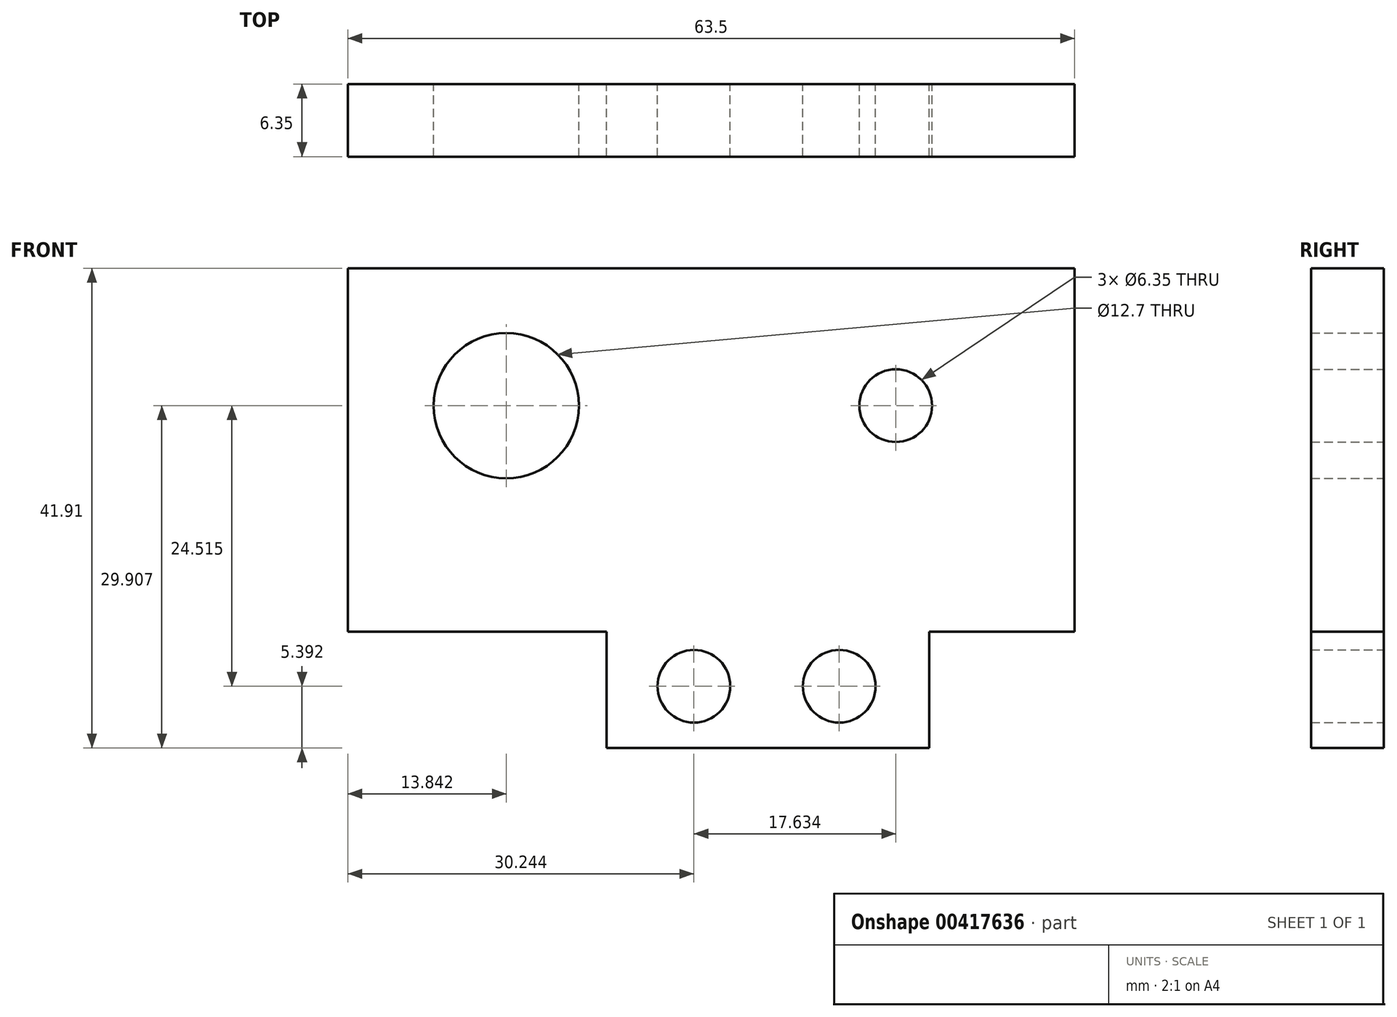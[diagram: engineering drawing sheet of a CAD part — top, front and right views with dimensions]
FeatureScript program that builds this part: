
annotation { "Feature Type Name" : "Feature", "Feature Type Description" : "" }
export const myFeature = defineFeature(function(context is Context, id is Id, definition is map)
    precondition{}
    {
        {
            var Q0;
            Q0=qCreatedBy(makeId("Front.planeOp"),FACE);
            var sketch = newSketch(context, id + "F0", { "sketchPlane" : qUnion([Q0])});
            skLineSegment(sketch, "E0", {"start": v(-23.02, 21.88) * mm, "end": v(40.48, 21.88) * mm});
            skLineSegment(sketch, "E1", {"start": v(-23.02, 21.88) * mm, "end": v(-23.02, -9.87) * mm});
            skLineSegment(sketch, "E2", {"start": v(-23.02, -9.87) * mm, "end": v(-0.4, -9.87) * mm});
            skLineSegment(sketch, "E3", {"start": v(-0.4, -9.87) * mm, "end": v(-0.4, -20.03) * mm});
            skLineSegment(sketch, "E4", {"start": v(-0.4, -20.03) * mm, "end": v(27.78, -20.03) * mm});
            skLineSegment(sketch, "E5", {"start": v(27.78, -20.03) * mm, "end": v(27.78, -9.87) * mm});
            skLineSegment(sketch, "E6", {"start": v(27.78, -9.87) * mm, "end": v(40.48, -9.87) * mm});
            skLineSegment(sketch, "E7", {"start": v(40.48, -9.87) * mm, "end": v(40.48, 21.88) * mm});
            skPoint(sketch, "E8.startSnap0", {"position": v(-11.71, -9.87) * mm});
            skPoint(sketch, "E9", {"position": v(7.22, -14.64) * mm});
            skPoint(sketch, "E10", {"position": v(19.92, -14.64) * mm});
            skPoint(sketch, "E11", {"position": v(-9.18, 9.88) * mm});
            skPoint(sketch, "E12", {"position": v(24.86, 9.88) * mm});
            skPoint(sketch, "E13", {"position": v(-0.4, -14.95) * mm});
            skPoint(sketch, "E14", {"position": v(27.78, -14.95) * mm});
            skLineSegment(sketch, "E15", {"start": v(-0.4, -14.95) * mm, "end": v(27.78, -14.95) * mm});
            skPoint(sketch, "E16", {"position": v(-23.02, 9.18) * mm});
            skPoint(sketch, "E17", {"position": v(40.48, 9.18) * mm});
            skLineSegment(sketch, "E18", {"start": v(-23.02, 9.18) * mm, "end": v(40.48, 9.18) * mm});
            skSolve(sketch);
        }
        {
            var Q0;
            Q0=makeQuery(id+"F0.imprint","IMPRINT",FACE,{"disambiguationData":[TD([[makeQuery(id+"F0.imprint","IMPRINT",EDGE,{"derivedFrom":sQuery(id+"F0.wireOp",EDGE,"E0")}),-1.0]])]});
            var Q1;
            {var subQ1=sQuery(id+"F0.wireOp",EDGE,"E2");Q1=makeQuery(id+"F0.imprint","IMPRINT",FACE,{"disambiguationData":[TD([[makeQuery(id+"F0.imprint","IMPRINT",EDGE,{"derivedFrom":subQ1}),1.0]])]});}
            var Q2;
            {var subQ0=sQuery(id+"F0.wireOp",EDGE,"E4");Q2=makeQuery(id+"F0.imprint","IMPRINT",FACE,{"disambiguationData":[TD([[makeQuery(id+"F0.imprint","IMPRINT",EDGE,{"derivedFrom":subQ0}),1.0]])]});}
            extrude(context, id + "F1", {"entities" : qUnion([Q0, Q1, Q2]), "depth" : 6.35 * mm});
        }
        {
            var Q0;
            Q0=sQuery(id+"F0.wireOp",VERTEX,"E11");
            var Q1;
            Q1=makeQuery(id+"F1.opExtrude","SWEPT_BODY",BODY,{"disambiguationData":[OSD([sQuery(id+"F0.wireOp",EDGE,"E0"),sQuery(id+"F0.wireOp",EDGE,"E1"),sQuery(id+"F0.wireOp",EDGE,"E2"),sQuery(id+"F0.wireOp",EDGE,"E3"),sQuery(id+"F0.wireOp",EDGE,"E4"),sQuery(id+"F0.wireOp",EDGE,"E5"),sQuery(id+"F0.wireOp",EDGE,"E6"),sQuery(id+"F0.wireOp",EDGE,"E7")])]});
            hole(context, id + "F2", {"style" : HoleStyle.SIMPLE, "endStyle" : HoleEndStyle.BLIND, "oppositeDirection" : true, "holeDiameter" : 12.7 * mm, "holeDepth" : 12.7 * mm, "isTappedThrough" : true, "tappedDepth" : 12.7 * mm, "tapClearance" : 3, "startFromSketch" : true, "locations" : qUnion([Q0]), "scope" : qUnion([Q1])});
        }
        {
            var Q0;
            Q0=sQuery(id+"F0.wireOp",VERTEX,"E12");
            var Q1;
            Q1=makeQuery(id+"F1.opExtrude","SWEPT_BODY",BODY,{"disambiguationData":[OSD([sQuery(id+"F0.wireOp",EDGE,"E0"),sQuery(id+"F0.wireOp",EDGE,"E1"),sQuery(id+"F0.wireOp",EDGE,"E2"),sQuery(id+"F0.wireOp",EDGE,"E3"),sQuery(id+"F0.wireOp",EDGE,"E4"),sQuery(id+"F0.wireOp",EDGE,"E5"),sQuery(id+"F0.wireOp",EDGE,"E6"),sQuery(id+"F0.wireOp",EDGE,"E7")])]});
            hole(context, id + "F3", {"style" : HoleStyle.SIMPLE, "endStyle" : HoleEndStyle.BLIND, "oppositeDirection" : true, "holeDiameter" : 6.35 * mm, "holeDepth" : 12.7 * mm, "isTappedThrough" : true, "tappedDepth" : 12.7 * mm, "tapClearance" : 3, "startFromSketch" : true, "locations" : qUnion([Q0]), "scope" : qUnion([Q1])});
        }
        {
            var Q0;
            Q0=sQuery(id+"F0.wireOp",VERTEX,"E9");
            var Q1;
            Q1=sQuery(id+"F0.wireOp",VERTEX,"E10");
            var Q2;
            Q2=makeQuery(id+"F1.opExtrude","SWEPT_BODY",BODY,{"disambiguationData":[OSD([sQuery(id+"F0.wireOp",EDGE,"E0"),sQuery(id+"F0.wireOp",EDGE,"E1"),sQuery(id+"F0.wireOp",EDGE,"E2"),sQuery(id+"F0.wireOp",EDGE,"E3"),sQuery(id+"F0.wireOp",EDGE,"E4"),sQuery(id+"F0.wireOp",EDGE,"E5"),sQuery(id+"F0.wireOp",EDGE,"E6"),sQuery(id+"F0.wireOp",EDGE,"E7")])]});
            hole(context, id + "F4", {"style" : HoleStyle.SIMPLE, "endStyle" : HoleEndStyle.BLIND, "oppositeDirection" : true, "holeDiameter" : 6.35 * mm, "holeDepth" : 12.7 * mm, "isTappedThrough" : true, "tappedDepth" : 12.7 * mm, "tapClearance" : 3, "startFromSketch" : true, "locations" : qUnion([Q0, Q1]), "scope" : qUnion([Q2])});
        }
    });
